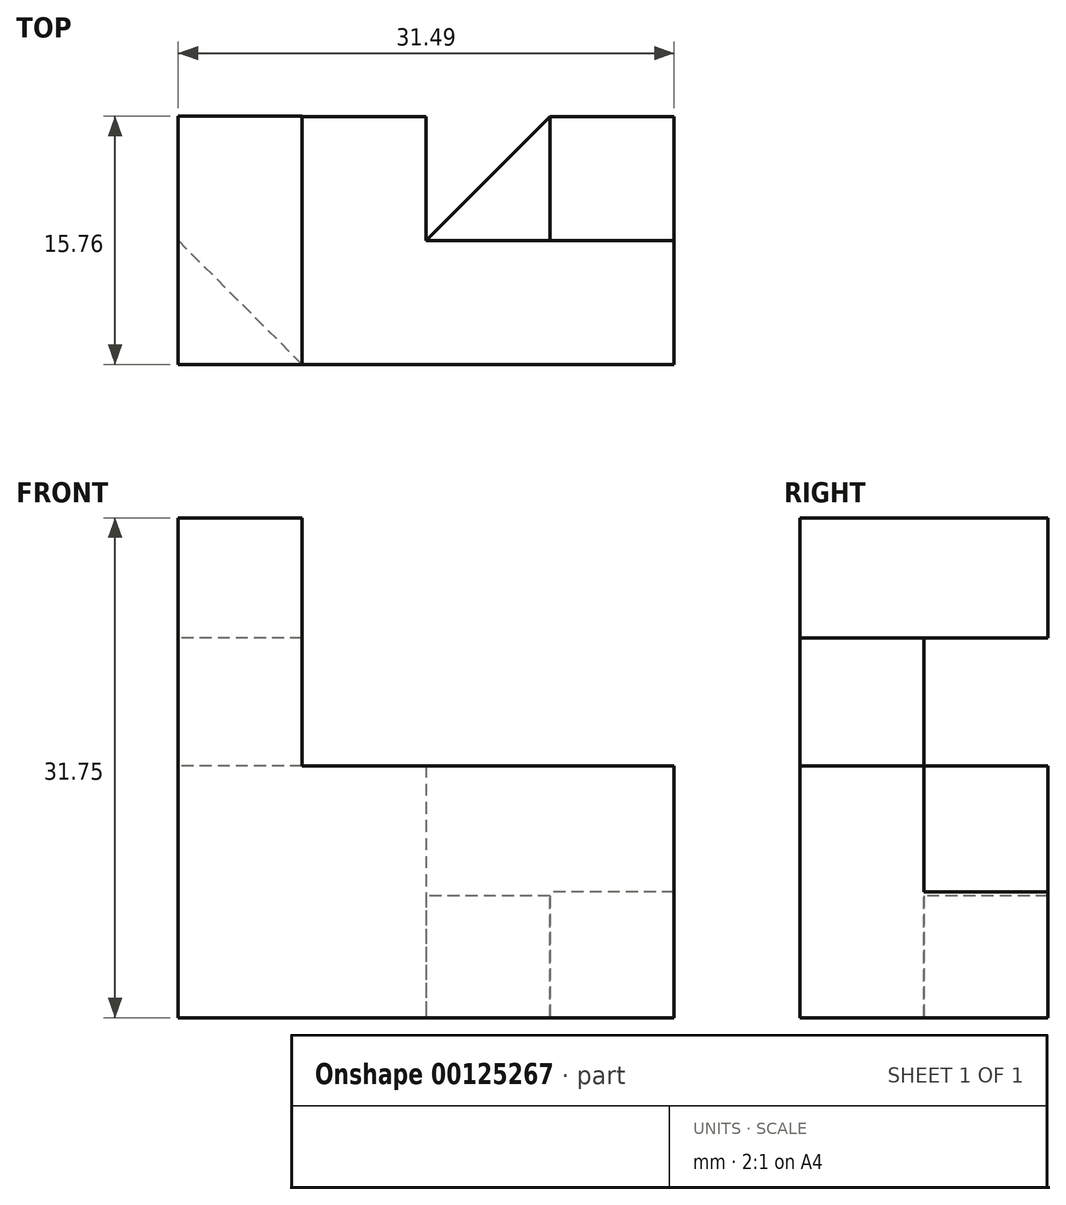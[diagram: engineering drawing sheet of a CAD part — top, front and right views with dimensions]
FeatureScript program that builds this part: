
annotation { "Feature Type Name" : "Feature", "Feature Type Description" : "" }
export const myFeature = defineFeature(function(context is Context, id is Id, definition is map)
    precondition{}
    {
        {
            var Q0;
            Q0=qCreatedBy(makeId("Top.planeOp"),FACE);
            var sketch = newSketch(context, id + "F0", { "sketchPlane" : qUnion([Q0])});
            skLineSegment(sketch, "E0.bottom", {"start": v(7.87, 7.87) * mm, "end": v(-7.87, 7.87) * mm});
            skLineSegment(sketch, "E0.top", {"start": v(7.87, -7.87) * mm, "end": v(-7.87, -7.87) * mm});
            skLineSegment(sketch, "E0.left", {"start": v(7.87, 7.87) * mm, "end": v(7.87, -7.87) * mm});
            skLineSegment(sketch, "E0.right", {"start": v(-7.87, 7.87) * mm, "end": v(-7.87, -7.87) * mm});
            skPoint(sketch, "E0.middle", {"position": v(0, 0) * mm});
            skSolve(sketch);
        }
        {
            var Q0;
            Q0=qSketchRegion(id+"F0",true);
            extrude(context, id + "F1", {"entities" : qUnion([Q0]), "depth" : 16 * mm});
        }
        {
            var Q0;
            Q0=makeQuery(id+"F1.opExtrude","CAP_FACE",FACE,{"disambiguationData":[OSD([sQuery(id+"F0.wireOp",EDGE,"E0.bottom"),sQuery(id+"F0.wireOp",EDGE,"E0.top"),sQuery(id+"F0.wireOp",EDGE,"E0.left"),sQuery(id+"F0.wireOp",EDGE,"E0.right")])],"isStart":false});
            var sketch = newSketch(context, id + "F2", { "sketchPlane" : qUnion([Q0])});
            skLineSegment(sketch, "E1", {"start": v(-7.87, 0) * mm, "end": v(-7.87, -7.87) * mm});
            skLineSegment(sketch, "E2", {"start": v(-7.87, -7.87) * mm, "end": v(0, -7.87) * mm});
            skLineSegment(sketch, "E3", {"start": v(0, -7.87) * mm, "end": v(-7.87, 0) * mm});
            skSolve(sketch);
        }
        {
            var Q0;
            Q0=makeQuery(id+"F2.imprint","IMPRINT",FACE,{"disambiguationData":[TD([[makeQuery(id+"F2.imprint","IMPRINT",EDGE,{"derivedFrom":sQuery(id+"F2.wireOp",EDGE,"E1")}),1.0]])]});
            extrude(context, id + "F3", {"entities" : qUnion([Q0]), "operationType" : NewBodyOperationType.ADD, "depth" : 8.13 * mm});
        }
        {
            var Q0;
            Q0=makeQuery(id+"F3.opExtrude","CAP_FACE",FACE,{"disambiguationData":[OSD([sQuery(id+"F2.wireOp",EDGE,"E1"),sQuery(id+"F2.wireOp",EDGE,"E2"),sQuery(id+"F2.wireOp",EDGE,"E3")])],"isStart":false});
            var sketch = newSketch(context, id + "F4", { "sketchPlane" : qUnion([Q0])});
            skLineSegment(sketch, "E4.bottom", {"start": v(-7.87, -7.87) * mm, "end": v(0, -7.87) * mm});
            skLineSegment(sketch, "E4.top", {"start": v(-7.87, 7.89) * mm, "end": v(0, 7.89) * mm});
            skLineSegment(sketch, "E4.left", {"start": v(-7.87, -7.87) * mm, "end": v(-7.87, 7.89) * mm});
            skLineSegment(sketch, "E4.right", {"start": v(0, -7.87) * mm, "end": v(0, 7.89) * mm});
            skSolve(sketch);
        }
        {
            var Q0;
            {var subQ0=sQuery(id+"F4.wireOp",EDGE,"E4.top");Q0=makeQuery(id+"F4.imprint","IMPRINT",FACE,{"disambiguationData":[TD([[makeQuery(id+"F4.imprint","IMPRINT",EDGE,{"derivedFrom":subQ0}),-1.0]])]});}
            var Q1;
            {var subQ0=sQuery(id+"F4.wireOp",EDGE,"E4.bottom");Q1=makeQuery(id+"F4.imprint","IMPRINT",FACE,{"disambiguationData":[TD([[makeQuery(id+"F4.imprint","IMPRINT",EDGE,{"derivedFrom":subQ0}),-1.0]])]});}
            extrude(context, id + "F5", {"entities" : qUnion([Q0, Q1]), "operationType" : NewBodyOperationType.ADD, "depth" : 7.62 * mm});
        }
        {
            var Q0;
            Q0=makeQuery(id+"F1.opExtrude","SWEPT_FACE",FACE,{"disambiguationData":[OSD([sQuery(id+"F0.wireOp",EDGE,"E0.left")])]});
            var sketch = newSketch(context, id + "F6", { "sketchPlane" : qUnion([Q0])});
            skLineSegment(sketch, "E5.bottom", {"start": v(-7.87, 16) * mm, "end": v(0, 16) * mm});
            skLineSegment(sketch, "E5.top", {"start": v(-7.87, 0) * mm, "end": v(0, 0) * mm});
            skLineSegment(sketch, "E5.left", {"start": v(-7.87, 16) * mm, "end": v(-7.87, 0) * mm});
            skLineSegment(sketch, "E5.right", {"start": v(0, 16) * mm, "end": v(0, 0) * mm});
            skSolve(sketch);
        }
        {
            var Q0;
            Q0=qSketchRegion(id+"F6",true);
            extrude(context, id + "F7", {"entities" : qUnion([Q0]), "operationType" : NewBodyOperationType.ADD, "depth" : 15.75 * mm});
        }
        {
            var Q0;
            Q0=makeQuery(id+"F7.opExtrude","SWEPT_FACE",FACE,{"disambiguationData":[OSD([sQuery(id+"F6.wireOp",EDGE,"E5.right")])]});
            var sketch = newSketch(context, id + "F8", { "sketchPlane" : qUnion([Q0])});
            skLineSegment(sketch, "E6.bottom", {"start": v(-23.62, 0) * mm, "end": v(-15.75, 0) * mm});
            skLineSegment(sketch, "E6.top", {"start": v(-23.62, 7.98) * mm, "end": v(-15.75, 7.98) * mm});
            skLineSegment(sketch, "E6.left", {"start": v(-23.62, 0) * mm, "end": v(-23.62, 7.98) * mm});
            skLineSegment(sketch, "E6.right", {"start": v(-15.75, 0) * mm, "end": v(-15.75, 7.98) * mm});
            skSolve(sketch);
        }
        {
            var Q0;
            Q0 = qSketchRegion(id + "F8", true);
            var Q1;
            Q1=makeQuery(id+"F1.opExtrude","SWEPT_FACE",FACE,{"disambiguationData":[OSD([sQuery(id+"F0.wireOp",EDGE,"E0.bottom")])]});
            extrude(context, id + "F9", {"entities" : qUnion([Q0]), "operationType" : NewBodyOperationType.ADD, "endBound" : BoundingType.UP_TO_SURFACE, "endBoundEntityFace" : qUnion([Q1]), "depth" : 25.4 * mm});
        }
        {
            var Q0;
            Q0=makeQuery(id+"F9.boolean.opBoolean","MERGE",FACE,{"derivedFrom":[makeQuery(id+"F7.boolean.opBoolean","MERGE",FACE,{"derivedFrom":[makeQuery(id+"F1.opExtrude","CAP_FACE",FACE,{"disambiguationData":[OSD([sQuery(id+"F0.wireOp",EDGE,"E0.bottom"),sQuery(id+"F0.wireOp",EDGE,"E0.top"),sQuery(id+"F0.wireOp",EDGE,"E0.left"),sQuery(id+"F0.wireOp",EDGE,"E0.right")])],"isStart":true}),makeQuery(id+"F7.opExtrude","SWEPT_FACE",FACE,{"disambiguationData":[OSD([sQuery(id+"F6.wireOp",EDGE,"E5.top")])]})]}),makeQuery(id+"F9.opExtrude","SWEPT_FACE",FACE,{"disambiguationData":[OSD([sQuery(id+"F8.wireOp",EDGE,"E6.bottom")])]})]});
            var sketch = newSketch(context, id + "F10", { "sketchPlane" : qUnion([Q0])});
            skLineSegment(sketch, "E7", {"start": v(15.75, -7.87) * mm, "end": v(7.87, 0) * mm});
            skLineSegment(sketch, "E8", {"start": v(15.75, -7.87) * mm, "end": v(15.75, 0) * mm});
            skLineSegment(sketch, "E9", {"start": v(15.75, 0) * mm, "end": v(7.87, 0) * mm});
            skSolve(sketch);
        }
        {
            var Q0;
            Q0 = qSketchRegion(id + "F10", true);
            var Q1;
            Q1=makeQuery(id+"F9.opExtrude","CAP_FACE",FACE,{"disambiguationData":[OSD([sQuery(id+"F0.wireOp",EDGE,"E0.bottom")])],"isStart":false});
            extrude(context, id + "F11", {"entities" : qUnion([Q0]), "oppositeDirection" : true, "endBoundEntityFace" : qUnion([Q1]), "depth" : 7.75 * mm});
        }
    });
